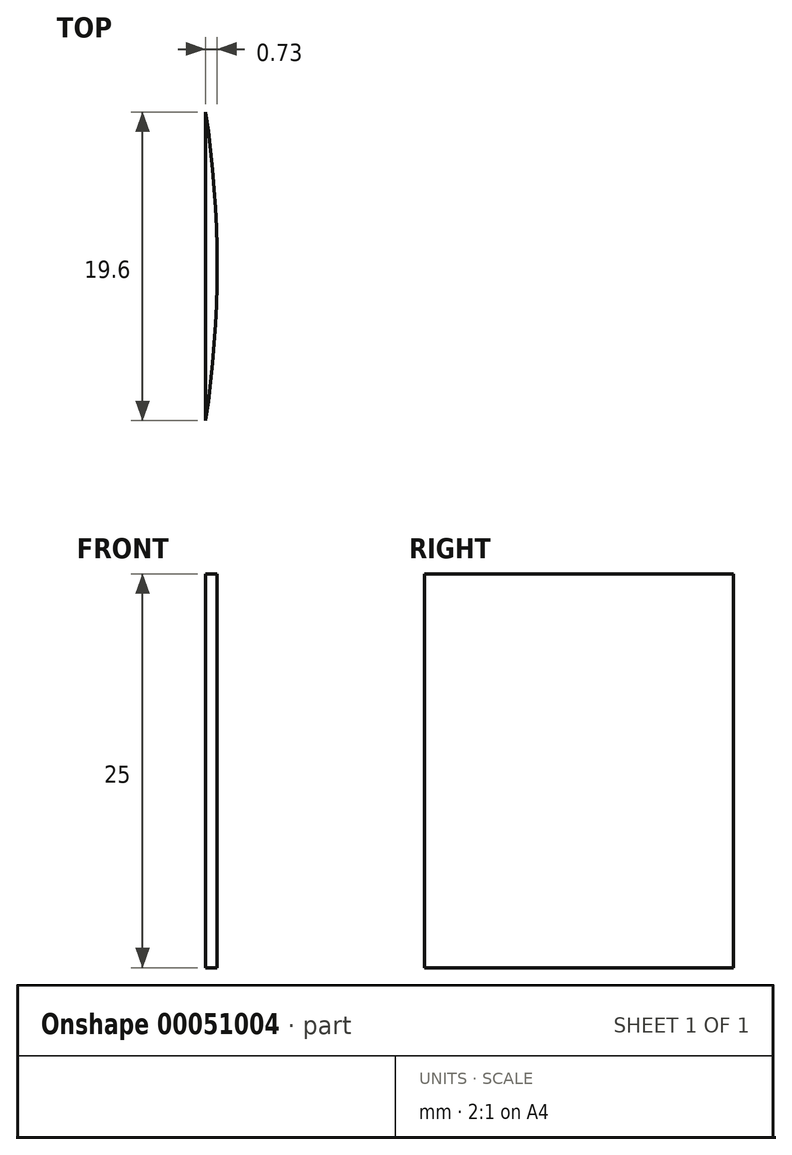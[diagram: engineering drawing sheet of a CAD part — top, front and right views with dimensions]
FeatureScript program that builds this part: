
annotation { "Feature Type Name" : "Feature", "Feature Type Description" : "" }
export const myFeature = defineFeature(function(context is Context, id is Id, definition is map)
    precondition{}
    {
        {
            var Q0;
            Q0=qCreatedBy(makeId("Top.planeOp"),FACE);
            var sketch = newSketch(context, id + "F0", { "sketchPlane" : qUnion([Q0])});
            skCircle(sketch, "E0", {"center": v(3.77, -4.2) * mm, "radius": 66.03 * mm});
            skText(sketch, "E1", { "text": "Gearbox", "fontName": "OpenSans-Bold.ttf"});
            const initialGuessF0  = {"E1": [-0.02693, -0.01615, 1, 0, 0.0282]};
            skSetInitialGuess(sketch, initialGuessF0);
            skSolve(sketch);
        }
        {
            var Q0;
            Q0=makeQuery(id+"F0.imprint","IMPRINT",FACE,{"disambiguationData":[TD([[makeQuery(id+"F0.imprint","IMPRINT",EDGE,{"derivedFrom":sQuery(id+"F0.wireOp",EDGE,"E0")}),1.0]])]});
            extrude(context, id + "F1", {"entities" : qUnion([Q0]), "depth" : 25 * mm});
        }
    });
